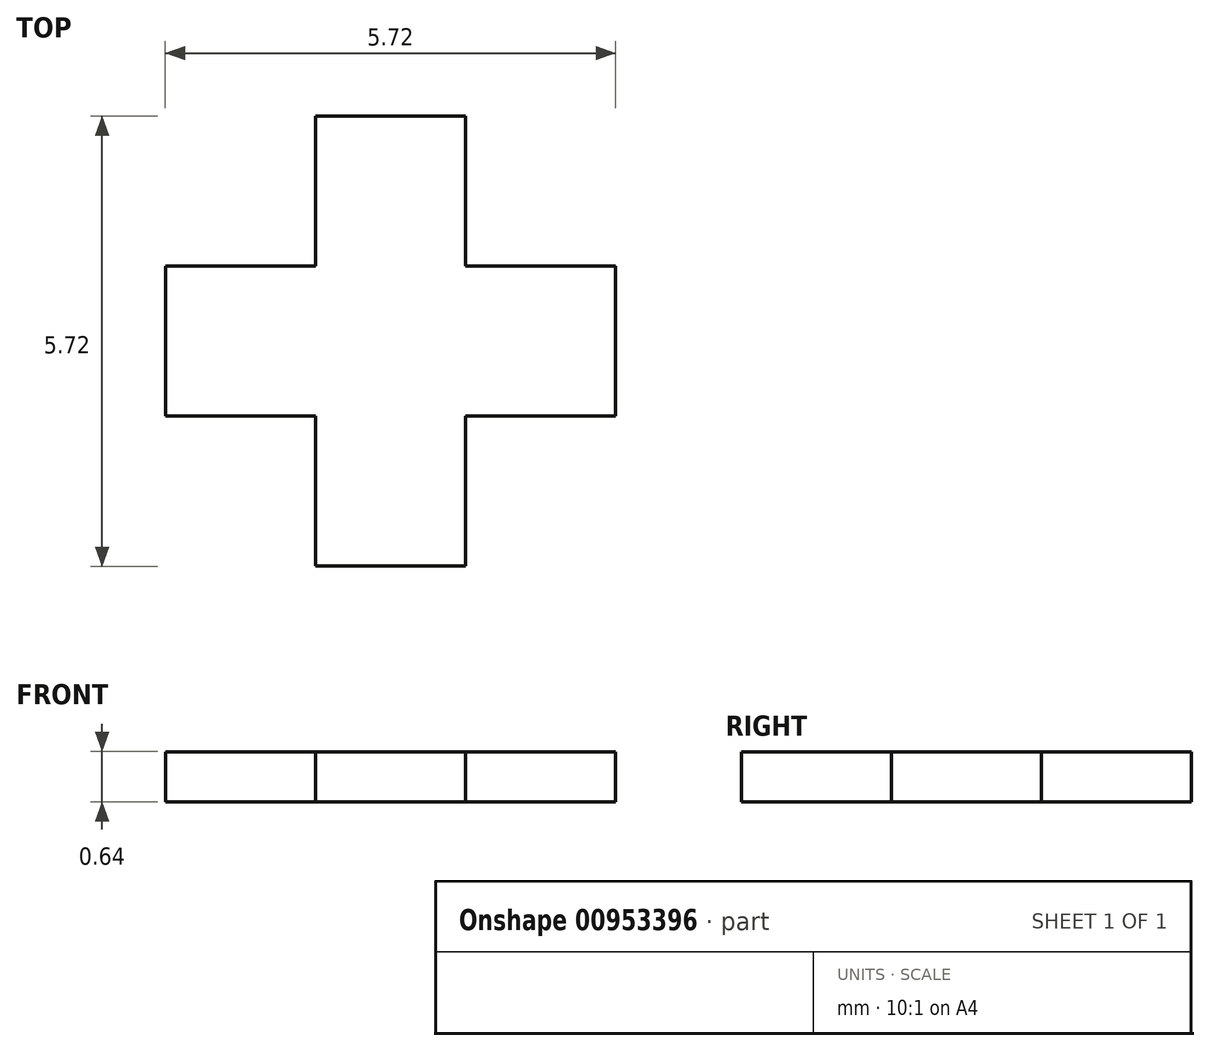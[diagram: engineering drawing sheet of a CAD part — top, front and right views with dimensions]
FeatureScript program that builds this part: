
annotation { "Feature Type Name" : "Feature", "Feature Type Description" : "" }
export const myFeature = defineFeature(function(context is Context, id is Id, definition is map)
    precondition{}
    {
        {
            var Q0;
            Q0=qCreatedBy(makeId("Top.planeOp"),FACE);
            var sketch = newSketch(context, id + "F0", { "sketchPlane" : qUnion([Q0])});
            skLineSegment(sketch, "E0", {"start": v(-33.75, -11.5) * mm, "end": v(-35.65, -11.5) * mm});
            skLineSegment(sketch, "E1", {"start": v(-35.65, -11.5) * mm, "end": v(-35.65, -13.4) * mm});
            skLineSegment(sketch, "E2", {"start": v(-35.65, -13.4) * mm, "end": v(-37.56, -13.4) * mm});
            skLineSegment(sketch, "E3", {"start": v(-37.56, -13.4) * mm, "end": v(-37.56, -15.3) * mm});
            skLineSegment(sketch, "E4", {"start": v(-37.56, -15.3) * mm, "end": v(-35.65, -15.3) * mm});
            skLineSegment(sketch, "E5", {"start": v(-35.65, -15.3) * mm, "end": v(-35.65, -17.2) * mm});
            skLineSegment(sketch, "E6", {"start": v(-35.65, -17.2) * mm, "end": v(-33.75, -17.2) * mm});
            skLineSegment(sketch, "E7", {"start": v(-33.75, -17.2) * mm, "end": v(-33.75, -15.3) * mm});
            skLineSegment(sketch, "E8", {"start": v(-33.75, -15.3) * mm, "end": v(-31.84, -15.3) * mm});
            skLineSegment(sketch, "E9", {"start": v(-31.84, -15.3) * mm, "end": v(-31.84, -13.4) * mm});
            skLineSegment(sketch, "E10", {"start": v(-31.84, -13.4) * mm, "end": v(-33.75, -13.4) * mm});
            skLineSegment(sketch, "E11", {"start": v(-33.75, -13.4) * mm, "end": v(-33.75, -11.5) * mm});
            skSolve(sketch);
        }
        {
            var Q0;
            Q0=qSketchRegion(id+"F0",true);
            extrude(context, id + "F1", {"entities" : qUnion([Q0]), "depth" : 0.64 * mm, "offsetDistance" : 25.4 * mm});
        }
    });
